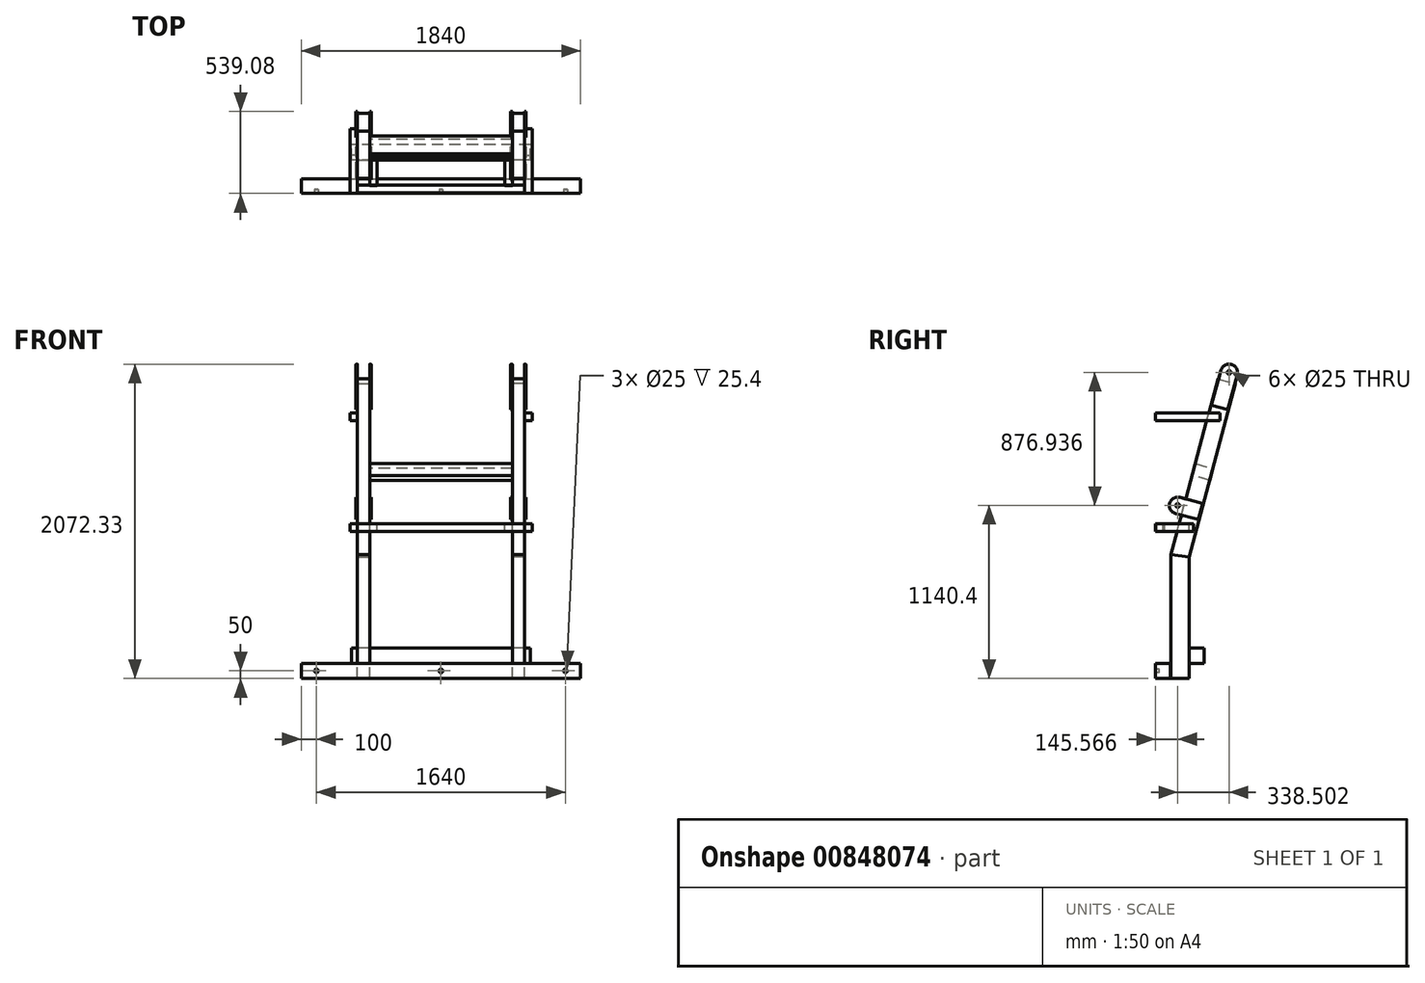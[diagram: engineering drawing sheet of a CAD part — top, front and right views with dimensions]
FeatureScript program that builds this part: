
annotation { "Feature Type Name" : "Feature", "Feature Type Description" : "" }
export const myFeature = defineFeature(function(context is Context, id is Id, definition is map)
    precondition{}
    {
        {
            var Q0;
            Q0=qCreatedBy(makeId("Front.planeOp"),FACE);
            var sketch = newSketch(context, id + "F0", { "sketchPlane" : qUnion([Q0])});
            skLineSegment(sketch, "E0.bottom", {"start": v(-920, 50) * mm, "end": v(920, 50) * mm});
            skLineSegment(sketch, "E0.top", {"start": v(-920, -50) * mm, "end": v(920, -50) * mm});
            skLineSegment(sketch, "E0.left", {"start": v(-920, 50) * mm, "end": v(-920, -50) * mm});
            skLineSegment(sketch, "E0.right", {"start": v(920, 50) * mm, "end": v(920, -50) * mm});
            skPoint(sketch, "E0.middle", {"position": v(0, 0) * mm});
            skSolve(sketch);
        }
        {
            var Q0;
            Q0=qCreatedBy(makeId("Front.planeOp"),FACE);
            var sketch = newSketch(context, id + "F1", { "sketchPlane" : qUnion([Q0])});
            skLineSegment(sketch, "E1", {"start": v(0, 0) * mm, "end": v(0, 945) * mm});
            skLineSegment(sketch, "E2.bottom", {"start": v(-550, 970) * mm, "end": v(550, 970) * mm});
            skLineSegment(sketch, "E2.top", {"start": v(-550, 920) * mm, "end": v(550, 920) * mm});
            skLineSegment(sketch, "E2.left", {"start": v(-550, 970) * mm, "end": v(-550, 920) * mm});
            skLineSegment(sketch, "E2.right", {"start": v(550, 970) * mm, "end": v(550, 920) * mm});
            skPoint(sketch, "E2.middle", {"position": v(0, 945) * mm});
            skSolve(sketch);
        }
        {
            var Q0;
            Q0=qCreatedBy(makeId("Front.planeOp"),FACE);
            var sketch = newSketch(context, id + "F2", { "sketchPlane" : qUnion([Q0])});
            skLineSegment(sketch, "E3", {"start": v(0, 0) * mm, "end": v(-550, 0) * mm});
            skLineSegment(sketch, "E4", {"start": v(-550, 0) * mm, "end": v(-550, 1650) * mm});
            skLineSegment(sketch, "E5.bottom", {"start": v(-550, 1650) * mm, "end": v(-600, 1650) * mm});
            skLineSegment(sketch, "E5.top", {"start": v(-550, 1700) * mm, "end": v(-600, 1700) * mm});
            skLineSegment(sketch, "E5.left", {"start": v(-550, 1650) * mm, "end": v(-550, 1700) * mm});
            skLineSegment(sketch, "E5.right", {"start": v(-600, 1650) * mm, "end": v(-600, 1700) * mm});
            skLineSegment(sketch, "E6.MirrorCS", {"start": v(600, 1650) * mm, "end": v(600, 1700) * mm});
            skLineSegment(sketch, "E7.MirrorCS", {"start": v(550, 1650) * mm, "end": v(600, 1650) * mm});
            skLineSegment(sketch, "E8.MirrorCS", {"start": v(550, 1650) * mm, "end": v(550, 1700) * mm});
            skLineSegment(sketch, "E9.MirrorCS", {"start": v(550, 1700) * mm, "end": v(600, 1700) * mm});
            skSolve(sketch);
        }
        {
            var Q0;
            Q0=qSketchRegion(id+"F0",true);
            extrude(context, id + "F3", {"entities" : qUnion([Q0]), "oppositeDirection" : true, "depth" : 97 * mm, "offsetDistance" : 25.4 * mm});
        }
        {
            var Q0;
            Q0=qSketchRegion(id+"F1",true);
            extrude(context, id + "F4", {"entities" : qUnion([Q0]), "oppositeDirection" : true, "depth" : 55 * mm, "offsetDistance" : 25.4 * mm, "hasSecondDirection" : true, "secondDirectionOppositeDirection" : true, "secondDirectionDepth" : 5 * mm});
        }
        {
            var Q0;
            Q0=qCreatedBy(makeId("Front.planeOp"),FACE);
            var sketch = newSketch(context, id + "F5", { "sketchPlane" : qUnion([Q0])});
            skLineSegment(sketch, "E10", {"start": v(0, 0) * mm, "end": v(-820, 0) * mm});
            skCircle(sketch, "E11", {"center": v(-820, 0) * mm, "radius": 12.5 * mm});
            skCircle(sketch, "E12", {"center": v(0, 0) * mm, "radius": 12.5 * mm});
            skCircle(sketch, "E13.MirrorC", {"center": v(820, 0) * mm, "radius": 12.5 * mm});
            skSolve(sketch);
        }
        {
            var Q0;
            Q0=qSketchRegion(id+"F5",true);
            extrude(context, id + "F6", {"entities" : qUnion([Q0]), "operationType" : NewBodyOperationType.REMOVE, "oppositeDirection" : true, "depth" : 25.4 * mm, "offsetDistance" : 25.4 * mm});
        }
        {
            var Q0;
            Q0=qCreatedBy(makeId("Front.planeOp"),FACE);
            var sketch = newSketch(context, id + "F7", { "sketchPlane" : qUnion([Q0])});
            skLineSegment(sketch, "E14", {"start": v(0, 0) * mm, "end": v(-550, 0) * mm});
            skLineSegment(sketch, "E15", {"start": v(-550, 0) * mm, "end": v(-550, 920) * mm});
            skLineSegment(sketch, "E16.bottom", {"start": v(-550, 920) * mm, "end": v(-600, 920) * mm});
            skLineSegment(sketch, "E16.top", {"start": v(-550, 970) * mm, "end": v(-600, 970) * mm});
            skLineSegment(sketch, "E16.left", {"start": v(-550, 920) * mm, "end": v(-550, 970) * mm});
            skLineSegment(sketch, "E16.right", {"start": v(-600, 920) * mm, "end": v(-600, 970) * mm});
            skLineSegment(sketch, "E17.MirrorCS", {"start": v(550, 920) * mm, "end": v(600, 920) * mm});
            skLineSegment(sketch, "E18.MirrorCS", {"start": v(600, 920) * mm, "end": v(600, 970) * mm});
            skLineSegment(sketch, "E19.MirrorCS", {"start": v(550, 970) * mm, "end": v(600, 970) * mm});
            skLineSegment(sketch, "E20.MirrorCS", {"start": v(550, 920) * mm, "end": v(550, 970) * mm});
            skSolve(sketch);
        }
        {
            var Q0;
            Q0=qSketchRegion(id+"F7",true);
            extrude(context, id + "F8", {"entities" : qUnion([Q0]), "oppositeDirection" : true, "depth" : 250 * mm, "offsetDistance" : 25 * mm});
        }
        {
            var Q0;
            Q0=qCreatedBy(makeId("Front.planeOp"),FACE);
            var sketch = newSketch(context, id + "F9", { "sketchPlane" : qUnion([Q0])});
            skLineSegment(sketch, "E21", {"start": v(0, 0) * mm, "end": v(-470, 0) * mm});
            skLineSegment(sketch, "E22", {"start": v(-470, 0) * mm, "end": v(-470, 920) * mm});
            skLineSegment(sketch, "E23.bottom", {"start": v(-470, 920) * mm, "end": v(-420, 920) * mm});
            skLineSegment(sketch, "E23.top", {"start": v(-470, 970) * mm, "end": v(-420, 970) * mm});
            skLineSegment(sketch, "E23.left", {"start": v(-470, 920) * mm, "end": v(-470, 970) * mm});
            skLineSegment(sketch, "E23.right", {"start": v(-420, 920) * mm, "end": v(-420, 970) * mm});
            skLineSegment(sketch, "E24.MirrorCS", {"start": v(470, 0) * mm, "end": v(470, 920) * mm});
            skLineSegment(sketch, "E25.MirrorCS", {"start": v(470, 920) * mm, "end": v(420, 920) * mm});
            skLineSegment(sketch, "E26.MirrorCS", {"start": v(470, 920) * mm, "end": v(470, 970) * mm});
            skLineSegment(sketch, "E27.MirrorCS", {"start": v(470, 970) * mm, "end": v(420, 970) * mm});
            skLineSegment(sketch, "E28.MirrorCS", {"start": v(420, 920) * mm, "end": v(420, 970) * mm});
            skSolve(sketch);
        }
        {
            var Q0;
            Q0=qSketchRegion(id+"F9",true);
            extrude(context, id + "F10", {"entities" : qUnion([Q0]), "oppositeDirection" : true, "depth" : 220 * mm, "offsetDistance" : 25 * mm, "hasSecondDirection" : true, "secondDirectionOppositeDirection" : true, "secondDirectionDepth" : 50 * mm});
        }
        {
            var Q0;
            Q0=qSketchRegion(id+"F2",true);
            extrude(context, id + "F11", {"entities" : qUnion([Q0]), "oppositeDirection" : true, "depth" : 425 * mm, "offsetDistance" : 25 * mm});
        }
        {
            var Q0;
            Q0=qCreatedBy(makeId("Right.planeOp"),FACE);
            var sketch = newSketch(context, id + "F12", { "sketchPlane" : qUnion([Q0])});
            skLineSegment(sketch, "E29", {"start": v(0, 0) * mm, "end": v(100, 0) * mm});
            skLineSegment(sketch, "E30.bottom", {"start": v(100, 0) * mm, "end": v(220, 0) * mm, "construction": true});
            skLineSegment(sketch, "E30.top", {"start": v(100, 750) * mm, "end": v(220, 750) * mm, "construction": true});
            skLineSegment(sketch, "E30.left", {"start": v(100, 0) * mm, "end": v(100, 750) * mm});
            skLineSegment(sketch, "E30.right", {"start": v(220, 0) * mm, "end": v(220, 750) * mm});
            skLineSegment(sketch, "E31", {"start": v(220, 750) * mm, "end": v(100, 765.8) * mm});
            skLineSegment(sketch, "E32", {"start": v(100, 750) * mm, "end": v(100, 765.8) * mm});
            skLineSegment(sketch, "E33", {"start": v(220, 0) * mm, "end": v(220, -50) * mm});
            skLineSegment(sketch, "E34", {"start": v(220, -50) * mm, "end": v(100, -50) * mm});
            skLineSegment(sketch, "E35", {"start": v(100, 0) * mm, "end": v(100, -50) * mm});
            skSolve(sketch);
        }
        {
            var Q0;
            Q0=qSketchRegion(id+"F12",true);
            extrude(context, id + "F13", {"entities" : qUnion([Q0]), "depth" : 550 * mm, "offsetDistance" : 25 * mm, "hasSecondDirection" : true, "secondDirectionOppositeDirection" : false, "secondDirectionDepth" : 470 * mm});
        }
        {
            var Q0;
            Q0=qCreatedBy(makeId("Right.planeOp"),FACE);
            var sketch = newSketch(context, id + "F14", { "sketchPlane" : qUnion([Q0])});
            skLineSegment(sketch, "E36", {"start": v(0, 0) * mm, "end": v(100, 0) * mm, "construction": true});
            skLineSegment(sketch, "E37", {"start": v(100, 0) * mm, "end": v(220, 0) * mm, "construction": true});
            skLineSegment(sketch, "E38", {"start": v(220, 0) * mm, "end": v(220, 750) * mm});
            skLineSegment(sketch, "E39", {"start": v(220, 750) * mm, "end": v(100, 750) * mm, "construction": true});
            skLineSegment(sketch, "E40", {"start": v(100, 750) * mm, "end": v(100, 0) * mm});
            skLineSegment(sketch, "E41", {"start": v(220, 750) * mm, "end": v(100, 765.8) * mm});
            skLineSegment(sketch, "E42", {"start": v(100, 750) * mm, "end": v(100, 765.8) * mm});
            skLineSegment(sketch, "E43", {"start": v(220, 0) * mm, "end": v(220, -50) * mm});
            skLineSegment(sketch, "E44", {"start": v(220, -50) * mm, "end": v(100, -50) * mm});
            skLineSegment(sketch, "E45", {"start": v(100, -50) * mm, "end": v(100, 0) * mm});
            skSolve(sketch);
        }
        {
            var Q0;
            Q0=qSketchRegion(id+"F14",true);
            extrude(context, id + "F15", {"entities" : qUnion([Q0]), "oppositeDirection" : true, "depth" : 550 * mm, "offsetDistance" : 25 * mm, "hasSecondDirection" : true, "secondDirectionOppositeDirection" : true, "secondDirectionDepth" : 470 * mm});
        }
        {
            var Q0;
            Q0=qCreatedBy(makeId("Right.planeOp"),FACE);
            var sketch = newSketch(context, id + "F16", { "sketchPlane" : qUnion([Q0])});
            skLineSegment(sketch, "E46", {"start": v(0, 0) * mm, "end": v(220, 0) * mm});
            skLineSegment(sketch, "E47", {"start": v(220, 0) * mm, "end": v(220, 750) * mm});
            skLineSegment(sketch, "E48", {"start": v(220, 750) * mm, "end": v(526.5, 1893.85) * mm});
            skLineSegment(sketch, "E49", {"start": v(0, 0) * mm, "end": v(0, 1850) * mm});
            skLineSegment(sketch, "E50", {"start": v(0, 1850) * mm, "end": v(475, 1850) * mm, "construction": true});
            skLineSegment(sketch, "E51", {"start": v(220, 750) * mm, "end": v(160, 750) * mm, "construction": true});
            skLineSegment(sketch, "E52", {"start": v(160, 750) * mm, "end": v(160, 0) * mm, "construction": true});
            skLineSegment(sketch, "E53", {"start": v(475, 1850) * mm, "end": v(475, 1913.1) * mm, "construction": true});
            skLineSegment(sketch, "E54", {"start": v(160, 750) * mm, "end": v(100, 750) * mm, "construction": true});
            skLineSegment(sketch, "E55", {"start": v(220, 750) * mm, "end": v(100, 765.8) * mm});
            skLineSegment(sketch, "E56", {"start": v(478.82, 1715.93) * mm, "end": v(420.86, 1731.45) * mm, "construction": true});
            skLineSegment(sketch, "E57", {"start": v(410.58, 1924.9) * mm, "end": v(100, 765.8) * mm, "construction": true});
            skLineSegment(sketch, "E58", {"start": v(420.86, 1731.45) * mm, "end": v(474.99, 1933.45) * mm, "construction": true});
            skPoint(sketch, "E59", {"position": v(474.99, 1933.45) * mm});
            skLineSegment(sketch, "E60", {"start": v(100, 765.8) * mm, "end": v(410.58, 1924.9) * mm});
            skLineSegment(sketch, "E61", {"start": v(410.58, 1924.9) * mm, "end": v(526.5, 1893.85) * mm});
            skSolve(sketch);
        }
        {
            var Q0;
            Q0=makeQuery(id+"F16.imprint","IMPRINT",FACE,{"disambiguationData":[TD([[makeQuery(id+"F16.imprint","IMPRINT",EDGE,{"derivedFrom":sQuery(id+"F16.wireOp",EDGE,"E48")}),1.0]])]});
            extrude(context, id + "F17", {"entities" : qUnion([Q0]), "depth" : 550 * mm, "offsetDistance" : 25 * mm, "hasSecondDirection" : true, "secondDirectionOppositeDirection" : false, "secondDirectionDepth" : 470 * mm});
        }
        {
            var Q0;
            Q0=qSketchRegion(id+"F16",true);
            extrude(context, id + "F18", {"entities" : qUnion([Q0]), "oppositeDirection" : true, "depth" : 550 * mm, "offsetDistance" : 25 * mm, "hasSecondDirection" : true, "secondDirectionOppositeDirection" : true, "secondDirectionDepth" : 470 * mm});
        }
        {
            var Q0;
            Q0=qCreatedBy(makeId("Right.planeOp"),FACE);
            var sketch = newSketch(context, id + "F19", { "sketchPlane" : qUnion([Q0])});
            skLineSegment(sketch, "E62", {"start": v(0, 0) * mm, "end": v(0, 1850) * mm});
            skLineSegment(sketch, "E63", {"start": v(0, 1850) * mm, "end": v(500, 1850) * mm});
            skLineSegment(sketch, "E64", {"start": v(521.67, 1895.14) * mm, "end": v(475.08, 1721.28) * mm});
            skLineSegment(sketch, "E65.0", {"start": v(410.58, 1924.9) * mm, "end": v(526.5, 1893.85) * mm});
            skLineSegment(sketch, "E66", {"start": v(468.54, 1909.38) * mm, "end": v(484.07, 1967.34) * mm, "construction": true});
            skCircle(sketch, "E67", {"center": v(484.07, 1967.34) * mm, "radius": 12.5 * mm});
            skLineSegment(sketch, "E68", {"start": v(537.2, 1953.1) * mm, "end": v(475.08, 1721.28) * mm});
            skLineSegment(sketch, "E69", {"start": v(475.08, 1721.28) * mm, "end": v(368.83, 1749.75) * mm});
            skLineSegment(sketch, "E70", {"start": v(368.83, 1749.75) * mm, "end": v(430.95, 1981.57) * mm});
            skArc(sketch, "E71", {"start": v(430.95, 1981.57) * mm, "mid": v(498.31, 2020.46) * mm, "end": v(537.2, 1953.1) * mm});
            skPoint(sketch, "E72", {"position": v(498.31, 2020.46) * mm});
            skSolve(sketch);
        }
        {
            var Q0;
            {var subQ5=sQuery(id+"F19.wireOp",EDGE,"E64");Q0=qUnion([makeQuery(id+"F19.imprint","IMPRINT",FACE,{"disambiguationData":[TD([[makeQuery(id+"F19.imprint","IMPRINT",EDGE,{"derivedFrom":subQ5}),-1.0]])]}),makeQuery(id+"F19.imprint","IMPRINT",FACE,{"disambiguationData":[TD([[makeQuery(id+"F19.imprint","IMPRINT",EDGE,{"derivedFrom":sQuery(id+"F19.wireOp",EDGE,"E67")}),-1.0]])]})]);}
            extrude(context, id + "F20", {"entities" : qUnion([Q0]), "operationType" : NewBodyOperationType.ADD, "depth" : 560 * mm, "offsetDistance" : 25 * mm, "hasSecondDirection" : true, "secondDirectionOppositeDirection" : false, "secondDirectionDepth" : 550 * mm});
        }
        {
            var Q0;
            {var subQ5=sQuery(id+"F19.wireOp",EDGE,"E64");Q0=qUnion([makeQuery(id+"F19.imprint","IMPRINT",FACE,{"disambiguationData":[TD([[makeQuery(id+"F19.imprint","IMPRINT",EDGE,{"derivedFrom":subQ5}),-1.0]])]}),makeQuery(id+"F19.imprint","IMPRINT",FACE,{"disambiguationData":[TD([[makeQuery(id+"F19.imprint","IMPRINT",EDGE,{"derivedFrom":sQuery(id+"F19.wireOp",EDGE,"E67")}),-1.0]])]})]);}
            extrude(context, id + "F21", {"entities" : qUnion([Q0]), "operationType" : NewBodyOperationType.ADD, "depth" : 470 * mm, "offsetDistance" : 25 * mm, "hasSecondDirection" : true, "secondDirectionOppositeDirection" : false, "secondDirectionDepth" : 460 * mm});
        }
        {
            var Q0;
            {var subQ5=sQuery(id+"F19.wireOp",EDGE,"E64");Q0=qUnion([makeQuery(id+"F19.imprint","IMPRINT",FACE,{"disambiguationData":[TD([[makeQuery(id+"F19.imprint","IMPRINT",EDGE,{"derivedFrom":subQ5}),-1.0]])]}),makeQuery(id+"F19.imprint","IMPRINT",FACE,{"disambiguationData":[TD([[makeQuery(id+"F19.imprint","IMPRINT",EDGE,{"derivedFrom":sQuery(id+"F19.wireOp",EDGE,"E67")}),-1.0]])]})]);}
            extrude(context, id + "F22", {"entities" : qUnion([Q0]), "operationType" : NewBodyOperationType.ADD, "oppositeDirection" : true, "depth" : 560 * mm, "offsetDistance" : 25 * mm, "hasSecondDirection" : true, "secondDirectionOppositeDirection" : true, "secondDirectionDepth" : 550 * mm});
        }
        {
            var Q0;
            {var subQ5=sQuery(id+"F19.wireOp",EDGE,"E64");Q0=qUnion([makeQuery(id+"F19.imprint","IMPRINT",FACE,{"disambiguationData":[TD([[makeQuery(id+"F19.imprint","IMPRINT",EDGE,{"derivedFrom":subQ5}),-1.0]])]}),makeQuery(id+"F19.imprint","IMPRINT",FACE,{"disambiguationData":[TD([[makeQuery(id+"F19.imprint","IMPRINT",EDGE,{"derivedFrom":sQuery(id+"F19.wireOp",EDGE,"E67")}),-1.0]])]})]);}
            extrude(context, id + "F23", {"entities" : qUnion([Q0]), "operationType" : NewBodyOperationType.ADD, "oppositeDirection" : true, "depth" : 470 * mm, "offsetDistance" : 25 * mm, "hasSecondDirection" : true, "secondDirectionOppositeDirection" : true, "secondDirectionDepth" : 460 * mm});
        }
        {
            var Q0;
            Q0=qCreatedBy(makeId("Right.planeOp"),FACE);
            var sketch = newSketch(context, id + "F24", { "sketchPlane" : qUnion([Q0])});
            skLineSegment(sketch, "E73", {"start": v(0, 1933.62) * mm, "end": v(0, 0) * mm, "construction": true});
            skCircle(sketch, "E74.0", {"center": v(484.07, 1967.34) * mm, "radius": 12.5 * mm});
            skLineSegment(sketch, "E75.0", {"start": v(100, 765.8) * mm, "end": v(410.58, 1924.9) * mm});
            skLineSegment(sketch, "E76.0", {"start": v(61.43, 776.42) * mm, "end": v(372.02, 1935.53) * mm, "construction": true});
            skLineSegment(sketch, "E77", {"start": v(484.07, 1967.34) * mm, "end": v(145.57, 1090.4) * mm, "construction": true});
            skCircle(sketch, "E78", {"center": v(145.57, 1090.4) * mm, "radius": 12.5 * mm});
            skLineSegment(sketch, "E79", {"start": v(145.57, 1090.4) * mm, "end": v(131.33, 1037.27) * mm, "construction": true});
            skLineSegment(sketch, "E80", {"start": v(131.33, 1037.27) * mm, "end": v(281.05, 997.16) * mm});
            skLineSegment(sketch, "E81", {"start": v(281.05, 997.16) * mm, "end": v(309.52, 1103.4) * mm});
            skLineSegment(sketch, "E82", {"start": v(309.52, 1103.4) * mm, "end": v(159.8, 1143.53) * mm});
            skArc(sketch, "E83", {"start": v(131.33, 1037.27) * mm, "mid": v(92.44, 1104.63) * mm, "end": v(159.8, 1143.53) * mm});
            skSolve(sketch);
        }
        {
            var Q0;
            Q0=qCreatedBy(makeId("Right.planeOp"),FACE);
            var sketch = newSketch(context, id + "F25", { "sketchPlane" : qUnion([Q0])});
            skLineSegment(sketch, "E84", {"start": v(0, 0) * mm, "end": v(220, 0) * mm});
            skLineSegment(sketch, "E85", {"start": v(220, 0) * mm, "end": v(220, 50) * mm});
            skLineSegment(sketch, "E86.bottom", {"start": v(220, 50) * mm, "end": v(320, 50) * mm});
            skLineSegment(sketch, "E86.top", {"start": v(220, 150) * mm, "end": v(320, 150) * mm});
            skLineSegment(sketch, "E86.left", {"start": v(220, 50) * mm, "end": v(220, 150) * mm});
            skLineSegment(sketch, "E86.right", {"start": v(320, 50) * mm, "end": v(320, 150) * mm});
            skSolve(sketch);
        }
        {
            var Q0;
            Q0=makeQuery(id+"F25.imprint","IMPRINT",FACE,{"disambiguationData":[TD([[makeQuery(id+"F25.imprint","IMPRINT",EDGE,{"derivedFrom":sQuery(id+"F25.wireOp",EDGE,"E86.bottom")}),1.0]])]});
            extrude(context, id + "F26", {"entities" : qUnion([Q0]), "depth" : 1180 / 2 * mm, "offsetDistance" : 25 * mm, "hasSecondDirection" : true, "secondDirectionOppositeDirection" : true, "secondDirectionDepth" : 590 * mm});
        }
        {
            var Q0;
            Q0=qSketchRegion(id+"F24",true);
            extrude(context, id + "F27", {"entities" : qUnion([Q0]), "depth" : 560 * mm, "offsetDistance" : 25 * mm, "hasSecondDirection" : true, "secondDirectionOppositeDirection" : false, "secondDirectionDepth" : 550 * mm});
        }
        {
            var Q0;
            Q0=qSketchRegion(id+"F24",true);
            extrude(context, id + "F28", {"entities" : qUnion([Q0]), "operationType" : NewBodyOperationType.ADD, "depth" : 470 * mm, "offsetDistance" : 25 * mm, "hasSecondDirection" : true, "secondDirectionOppositeDirection" : false, "secondDirectionDepth" : 460 * mm});
        }
        {
            var Q0;
            Q0=qSketchRegion(id+"F24",true);
            extrude(context, id + "F29", {"entities" : qUnion([Q0]), "oppositeDirection" : true, "depth" : 560 * mm, "offsetDistance" : 25 * mm, "hasSecondDirection" : true, "secondDirectionOppositeDirection" : true, "secondDirectionDepth" : 550 * mm});
        }
        {
            var Q0;
            Q0=qSketchRegion(id+"F24",true);
            extrude(context, id + "F30", {"entities" : qUnion([Q0]), "operationType" : NewBodyOperationType.ADD, "oppositeDirection" : true, "depth" : 470 * mm, "offsetDistance" : 25 * mm, "hasSecondDirection" : true, "secondDirectionOppositeDirection" : true, "secondDirectionDepth" : 460 * mm});
        }
        {
            var Q0;
            Q0=qCreatedBy(makeId("Right.planeOp"),FACE);
            var sketch = newSketch(context, id + "F31", { "sketchPlane" : qUnion([Q0])});
            skLineSegment(sketch, "E87", {"start": v(0, 0) * mm, "end": v(220, 0) * mm});
            skLineSegment(sketch, "E88", {"start": v(220, 0) * mm, "end": v(220, 750) * mm});
            skLineSegment(sketch, "E89", {"start": v(220, 750) * mm, "end": v(367.73, 1295.34) * mm, "construction": true});
            skLineSegment(sketch, "E90", {"start": v(367.73, 1295.34) * mm, "end": v(357.28, 1256.74) * mm});
            skLineSegment(sketch, "E91", {"start": v(357.28, 1256.74) * mm, "end": v(241.45, 1288.11) * mm});
            skLineSegment(sketch, "E92", {"start": v(241.45, 1288.11) * mm, "end": v(262.37, 1365.33) * mm});
            skLineSegment(sketch, "E93", {"start": v(262.37, 1365.33) * mm, "end": v(378.2, 1333.95) * mm});
            skLineSegment(sketch, "E94", {"start": v(378.2, 1333.95) * mm, "end": v(367.73, 1295.34) * mm});
            skSolve(sketch);
        }
        {
            var Q0;
            Q0=qSketchRegion(id+"F31",true);
            extrude(context, id + "F32", {"entities" : qUnion([Q0]), "depth" : 940 / 2 * mm, "offsetDistance" : 25 * mm, "hasSecondDirection" : true, "secondDirectionOppositeDirection" : true, "secondDirectionDepth" : 470 * mm});
        }
    });
